# Revit family: 8329, 8331 Boston 600
name_source: partatom
category: Lighting Fixtures
revit_build: Autodesk Revit 2018 (Build: 20170223_1515(x64)
units: mm (PartAtom-declared; Revit-internal decimal feet)

## family parameters
Always vertical = Yes
Cut with Voids When Loaded = No
Host = Wall
Light Source = Yes
OmniClass Number = 23.80.70.00
OmniClass Title = Lighting
Part Type = Normal
Room Calculation Point = No
Round Connector Dimension = Use Diameter
Shared = No

## types (2) — shared parameters
Color Filter = 16777215
Dimming Lamp Color Temperature Shift = <None>
Driver Required = No
Main Material = Metal - Steel
Manufacturer = Astro Lighting Ltd
Tilt Angle = 60.00°
URL = www.astrolighting.com

## per-type parameters (varying)
| type | ADA compliant | Dimmable | Driver Included | Efficacy (lm/w) | Electrical Class | Lamp | Light Source Fixed | Location rating | Photometric Web File | Power (Watts) | Product Code | Product Location | Product Name | Product SKU |
| CE |  | No | Yes | 37.03 | 2 | Dedicated LED | Yes | IP44 | GNC-21152 Boston 600.ies | 21.9 | 8329 | Bathroom / Indoor | Boston 600 | 1370003 |
| ETL | NO |  |  |  | 0 |  |  | DAMP | generic |  | 1234 | Bathroom |  | 1234001 |

## geometry (parser evidence)
native form markers: Sweep x1
no freeform markers — native parametric forms only
